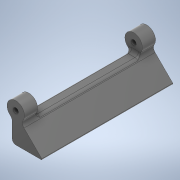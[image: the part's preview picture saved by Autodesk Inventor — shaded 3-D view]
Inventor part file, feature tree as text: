
AUTODESK INVENTOR PART (.ipt)
format: ipt  version: 2020.2 (Build 242310000, 310)  size: 287,232 bytes
history: native  units: mm
features: extrude x5, sketch x4, projected_geometry x3, plane x2, fillet x2, mirror x1
ambient origin geometry x8: Origin, YZ Plane, XZ Plane, XY Plane, X Axis, Y Axis, Z Axis, Center Point
bodies: Solid1 (feature_tree)
feature tree (17):
  extrude  "Extrusion1"  Depth=2.0mm
  plane  "Work Plane1"
  fillet  "Fillet1"  Radius=17.0mm
  extrude  "Extrusion3"  TaperAngle=45.0deg  [1 undecoded]
  extrude  "Extrusion4"  Depth=3.0mm
  fillet  "Fillet2"  Radius=3.0mm
  mirror  "Mirror2"
  extrude  "Extrusion5"  Depth=10.0mm
  plane  "Work Plane2"
  extrude  "Extrusion6"  Depth=10.0mm
  sketch  "Sketch1"  dims[d0=3.0mm d1=2.0mm d2=17.0mm]
  sketch  "Sketch3"  dims[d3=10.0mm d4=45.0deg]
  projected_geometry  "Projected Loop1"
  sketch  "Sketch4"  dims[d5=0.5mm d6=3.0mm d7=3.0mm]
  projected_geometry  "Projected Loop2"
  projected_geometry  "Projected Loop3"
  sketch  "Sketch6"  dims[d8=3.5mm d9=10.0mm d10=3.5mm d11=5.5mm d12=7.5mm d13=0.0mm d18=3.0mm d19=45.0deg d20=1.5mm d21=0.35mm d22=0.0mm d23=12.0mm d24=30.0mm d25=0.0mm d26=22.68928mm d27=8.0mm d28=10.0mm d29=0.0mm d30=2.0mm d31=1.0mm d32=1.7mm d33=1.7mm d34=26.0mm d35=24.375mm d36=10.0mm d37=0.0mm d38=7.5mm d40=-6.0mm d41=3.5mm d42=3.5mm d43=10.0mm d44=0.0mm d45=0.5mm d46=0.872665mm d47=0.5mm d48=0.872665mm]
note: 1 required parameter value undecoded (feature->parameter linkage not recoverable at this tier; creation-order binding heuristic only, values carry confidence <= 0.55)
